# Revit family: M_Ceiling Light - Flat Round
name_source: partatom
category: Lighting Fixtures
revit_build: Autodesk Revit 2017 (Build: 20160109_1515(x64)
units: mm (PartAtom-declared; Revit-internal decimal feet)

## family parameters
Always vertical = Yes
Cut with Voids When Loaded = No
Host = Ceiling
Light Source = Yes
OmniClass Number = 23.80.70.11.11
OmniClass Title = General Luminaries, Non Directional
Part Type = Normal
Room Calculation Point = No
Round Connector Dimension = Use Diameter
Shared = No

## types (4) — shared parameters
Assembly Code = D5020220
Ballast Number of Poles = 1
Color Filter = 16777215
Diffuser Material = Glass, White, High Luminance
Dimming Lamp Color Temperature Shift = <None>
Emit Shape Visible in Rendering = No
Emit from Circle Diameter = 250 mm  [stored 0.82021 ft]
Lamp = A-19
Light Box Material = Steel, Paint Finish, Dark Gray, Matte
Light Source Symbol Size = 610 mm
Load Classification = Lighting - Dwelling Unit

## per-type parameters (varying)
| type | Apparent Load | Ballast Voltage |
| 60W - 120V | 60 VA | 120 V |
| 60W - 277V | 60 VA | 277 V |
| 100W - 120V | 100 VA | 120 V |
| 100W - 277V | 100 VA | 277 V |

note: [stored X ft] marks values corroborated as IEEE doubles in the binary element streams (Revit-internal decimal feet)

## geometry (parser evidence)
native form markers: Sweep x1
no freeform markers — native parametric forms only
